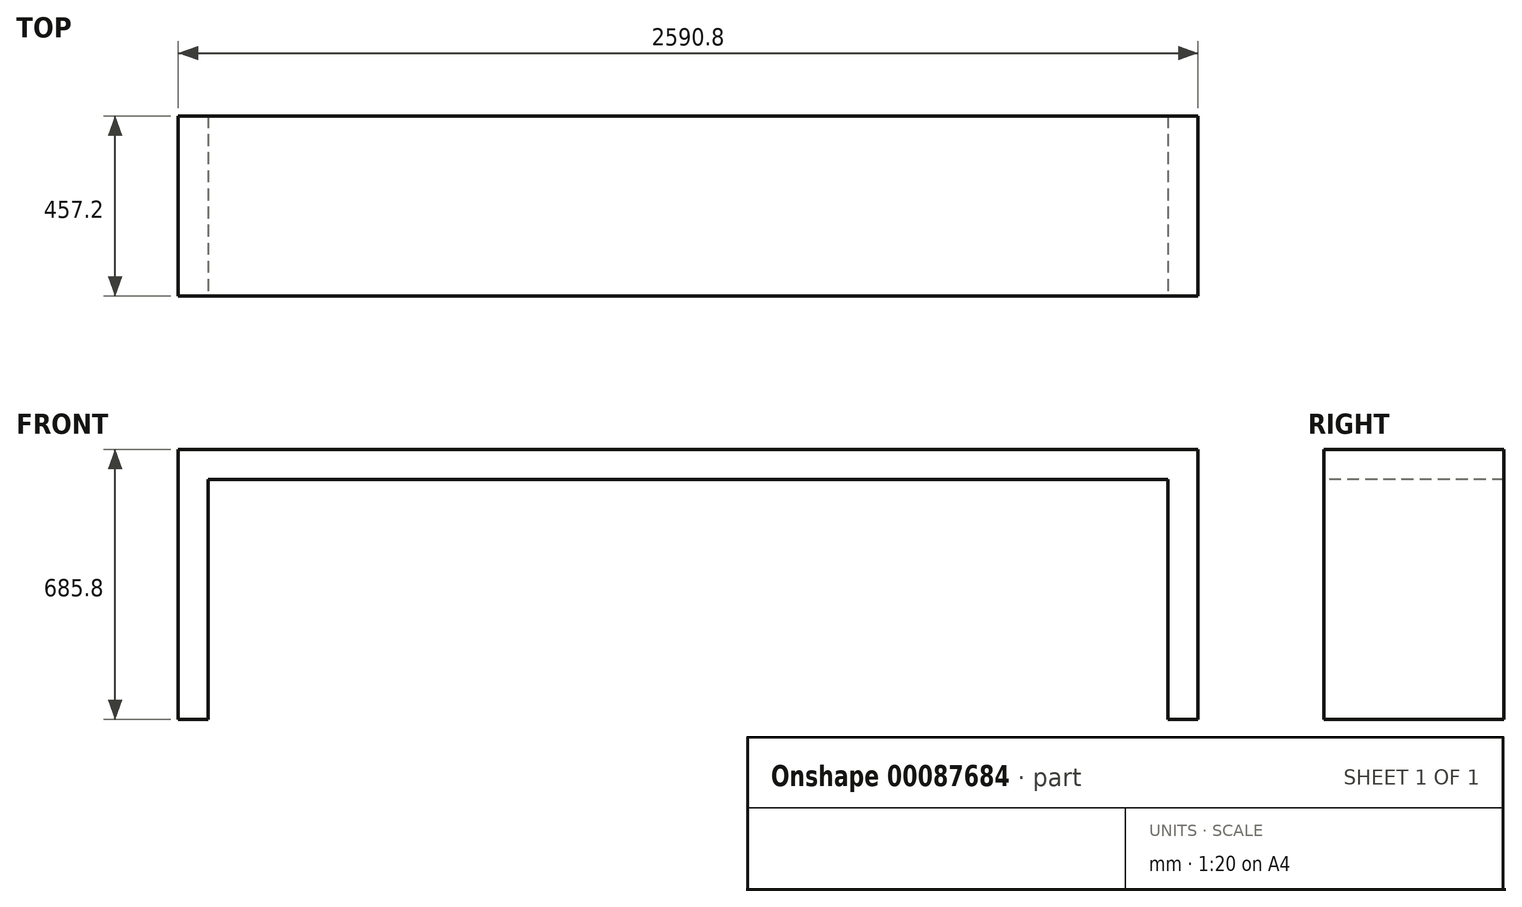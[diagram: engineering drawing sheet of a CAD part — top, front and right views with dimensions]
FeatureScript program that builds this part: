
annotation { "Feature Type Name" : "Feature", "Feature Type Description" : "" }
export const myFeature = defineFeature(function(context is Context, id is Id, definition is map)
    precondition{}
    {
        {
            var Q0;
            Q0=qCreatedBy(makeId("Top.planeOp"),FACE);
            var sketch = newSketch(context, id + "F0", { "sketchPlane" : qUnion([Q0])});
            skLineSegment(sketch, "E0.bottom", {"start": v(-2897.27, -1894.61) * mm, "end": v(-458.87, -1894.61) * mm});
            skLineSegment(sketch, "E0.top", {"start": v(-2897.27, -2351.81) * mm, "end": v(-458.87, -2351.81) * mm});
            skLineSegment(sketch, "E0.left", {"start": v(-2897.27, -1894.61) * mm, "end": v(-2897.27, -2351.81) * mm});
            skLineSegment(sketch, "E0.right", {"start": v(-458.87, -1894.61) * mm, "end": v(-458.87, -2351.81) * mm});
            skSolve(sketch);
        }
        {
            var Q0;
            Q0=qSketchRegion(id+"F0",true);
            extrude(context, id + "F1", {"entities" : qUnion([Q0]), "depth" : 609.6 * mm});
        }
        {
            var Q0;
            Q0=makeQuery(id+"F1.opExtrude","SWEPT_FACE",FACE,{"disambiguationData":[OSD([sQuery(id+"F0.wireOp",EDGE,"E0.top")])]});
            var Q1;
            Q1=makeQuery(id+"F1.opExtrude","SWEPT_FACE",FACE,{"disambiguationData":[OSD([sQuery(id+"F0.wireOp",EDGE,"E0.bottom")])]});
            var Q2;
            Q2=makeQuery(id+"F1.opExtrude","CAP_FACE",FACE,{"disambiguationData":[OSD([sQuery(id+"F0.wireOp",EDGE,"E0.bottom"),sQuery(id+"F0.wireOp",EDGE,"E0.top"),sQuery(id+"F0.wireOp",EDGE,"E0.left"),sQuery(id+"F0.wireOp",EDGE,"E0.right")])],"isStart":true});
            shell(context, id + "F2", {"entities" : qUnion([Q0, Q1, Q2]), "thickness" : 76.2 * mm, "oppositeDirection" : true});
        }
    });
